# Revit family: YGNIS_Caldera de condensación LRK
name_source: partatom
category: Equipos mecánicos
revit_build: Autodesk Revit 2016 (Build: 20150220_1215(x64)
units: mm (PartAtom-declared; Revit-internal decimal feet)

## family parameters
Compartido = No
Corte con vacíos al cargar = No
Cota de conector redondo = Diámetro de uso
Número OmniClass = 23.75.00.00
Punto de cálculo de habitación = No
Se basa en plano de trabajo = No
Siempre vertical = Sí
Tipo de pieza = Normal
Título OmniClass = Climate Control (HVAC)

## types (10) — shared parameters
Asas = 580 mm
Código de montaje = D3020100
Descripción = Calderas de condensación para gas
o gasóleo 3 pasos de humos
Fabricante = YGNIS Atlantic
Presión de servicio = 5.9 atm
URL = http://www.ygnis.es

## per-type parameters (varying)
- LRK 23: B=1180 mm; H=1450 mm; L=2700 mm; Modelo=LRK 23; Peso=1800.00 kg; Potencia 30/35ºC=709 kW; Potencia 80/60ºC=630 kW; Potencia útil condensador=79 kW; Volumen=690.0 L; a=145 mm  [stored 0.475722 ft]; b=1060 mm; c=800 mm; d1=690 mm; d2=240 mm  [stored 0.787402 ft]; e=250 mm  [stored 0.82021 ft]; e. ext=300 mm; e. int=245 mm  [stored 0.803806 ft]; f=60 mm  [stored 0.19685 ft]; g=100 mm  [stored 0.328084 ft]; h=1370 mm; i=150 mm; j=950 mm; k=100 mm  [stored 0.328084 ft]; l=1695 mm; m=285 mm; n=80 mm  [stored 0.262467 ft]; n.2=180 mm; o=475 mm; q=85 mm  [stored 0.278871 ft]; q.2=30 mm  [stored 0.0984252 ft]; ø empalme ida-retorno=200 mm  [stored 0.656168 ft]
- LRK 24: B=1250 mm; H=1535 mm; L=2960 mm; Modelo=LRK 24; Peso=2160.00 kg; Potencia 30/35ºC=787 kW; Potencia 80/60ºC=700 kW; Potencia útil condensador=87 kW; Volumen=840.0 L; a=145 mm  [stored 0.475722 ft]; b=1130 mm; c=875 mm; d1=740 mm; d2=305 mm  [stored 1.00066 ft]; e=250 mm  [stored 0.82021 ft]; e. ext=300 mm; e. int=245 mm  [stored 0.803806 ft]; f=60 mm  [stored 0.19685 ft]; g=100 mm  [stored 0.328084 ft]; h=1455 mm; i=200 mm  [stored 0.656168 ft]; j=1150 mm; k=115 mm  [stored 0.377297 ft]; l=1880 mm; m=305 mm  [stored 1.00066 ft]; n=80 mm  [stored 0.262467 ft]; n.2=180 mm; o=560 mm; q=125 mm  [stored 0.410105 ft]; q.2=70 mm  [stored 0.229659 ft]; ø empalme ida-retorno=200 mm  [stored 0.656168 ft]
- LRK 25: B=1250 mm; H=1535 mm; L=2960 mm; Modelo=LRK 25; Peso=2160.00 kg; Potencia 30/35ºC=901 kW; Potencia 80/60ºC=800 kW; Potencia útil condensador=101 kW; Volumen=840.0 L; a=145 mm  [stored 0.475722 ft]; b=1130 mm; c=875 mm; d1=740 mm; d2=305 mm  [stored 1.00066 ft]; e=250 mm  [stored 0.82021 ft]; e. ext=300 mm; e. int=245 mm  [stored 0.803806 ft]; f=60 mm  [stored 0.19685 ft]; g=100 mm  [stored 0.328084 ft]; h=1455 mm; i=200 mm  [stored 0.656168 ft]; j=1150 mm; k=115 mm  [stored 0.377297 ft]; l=1880 mm; m=305 mm  [stored 1.00066 ft]; n=80 mm  [stored 0.262467 ft]; n.2=180 mm; o=560 mm; q=125 mm  [stored 0.410105 ft]; q.2=70 mm  [stored 0.229659 ft]; ø empalme ida-retorno=200 mm  [stored 0.656168 ft]
- LRK 26: B=1330 mm; H=1625 mm; L=3130 mm; Modelo=LRK 26; Peso=2420.00 kg; Potencia 30/35ºC=1005 kW; Potencia 80/60ºC=895 kW; Potencia útil condensador=110 kW; Volumen=1020.0 L; a=145 mm  [stored 0.475722 ft]; b=1210 mm; c=950 mm; d1=790 mm; d2=355 mm; e=300 mm; e. ext=350 mm  [stored 1.14829 ft]; e. int=295 mm  [stored 0.967848 ft]; f=60 mm  [stored 0.19685 ft]; g=100 mm  [stored 0.328084 ft]; h=1545 mm; i=200 mm  [stored 0.656168 ft]; j=1150 mm; k=125 mm  [stored 0.410105 ft]; l=1975 mm; m=335 mm  [stored 1.09908 ft]; n=100 mm  [stored 0.328084 ft]; n.2=200 mm  [stored 0.656168 ft]; o=650 mm; q=165 mm; q.2=110 mm  [stored 0.360892 ft]; ø empalme ida-retorno=200 mm  [stored 0.656168 ft]
- LRK 27: B=1420 mm; H=1730 mm; L=3624 mm; Modelo=LRK 27; Peso=2950.00 kg; Potencia 30/35ºC=1293 kW; Potencia 80/60ºC=1150 kW; Potencia útil condensador=143 kW; Volumen=1430.0 L; a=145 mm  [stored 0.475722 ft]; b=1300 mm; c=1105 mm; d1=840 mm; d2=400 mm; e=350 mm  [stored 1.14829 ft]; e. ext=400 mm; e. int=345 mm  [stored 1.13189 ft]; f=60 mm  [stored 0.19685 ft]; g=125 mm  [stored 0.410105 ft]; h=1650 mm; i=238 mm  [stored 0.78084 ft]; j=1493 mm; k=110 mm  [stored 0.360892 ft]; l=2314 mm; m=385 mm  [stored 1.26312 ft]; n=100 mm  [stored 0.328084 ft]; n.2=200 mm  [stored 0.656168 ft]; o=720 mm; q=185 mm  [stored 0.606955 ft]; q.2=130 mm  [stored 0.426509 ft]; ø empalme ida-retorno=225 mm  [stored 0.738189 ft]
- LRK 28: B=1420 mm; H=1730 mm; L=3624 mm; Modelo=LRK 28; Peso=2950.00 kg; Potencia 30/35ºC=1463 kW; Potencia 80/60ºC=1300 kW; Potencia útil condensador=164 kW; Volumen=1430.0 L; a=145 mm  [stored 0.475722 ft]; b=1300 mm; c=1105 mm; d1=840 mm; d2=400 mm; e=350 mm  [stored 1.14829 ft]; e. ext=400 mm; e. int=345 mm  [stored 1.13189 ft]; f=60 mm  [stored 0.19685 ft]; g=125 mm  [stored 0.410105 ft]; h=1650 mm; i=238 mm  [stored 0.78084 ft]; j=1493 mm; k=110 mm  [stored 0.360892 ft]; l=2314 mm; m=385 mm  [stored 1.26312 ft]; n=100 mm  [stored 0.328084 ft]; n.2=200 mm  [stored 0.656168 ft]; o=720 mm; q=185 mm  [stored 0.606955 ft]; q.2=130 mm  [stored 0.426509 ft]; ø empalme ida-retorno=225 mm  [stored 0.738189 ft]
- LRK 29: B=1495 mm; H=1805 mm; L=4194 mm; Modelo=LRK 29; Peso=3508.00 kg; Potencia 30/35ºC=1858 kW; Potencia 80/60ºC=1650 kW; Potencia útil condensador=208 kW; Volumen=1885.0 L; a=200 mm  [stored 0.656168 ft]; b=1375 mm; c=1260 mm; d1=875 mm; d2=448 mm; e=350 mm  [stored 1.14829 ft]; e. ext=400 mm; e. int=345 mm  [stored 1.13189 ft]; f=60 mm  [stored 0.19685 ft]; g=125 mm  [stored 0.410105 ft]; h=1725 mm; i=274 mm  [stored 0.89895 ft]; j=1727 mm; k=107 mm  [stored 0.35105 ft]; l=2374 mm; m=455 mm; n=125 mm  [stored 0.410105 ft]; n.2=225 mm  [stored 0.738189 ft]; o=795 mm; q=235 mm  [stored 0.770997 ft]; q.2=180 mm; ø empalme ida-retorno=225 mm  [stored 0.738189 ft]
- LRK 30: B=1565 mm; H=1870 mm; L=4579 mm; Modelo=LRK 30; Peso=4133.00 kg; Potencia 30/35ºC=2139 kW; Potencia 80/60ºC=1900 kW; Potencia útil condensador=239 kW; Volumen=2170.0 L; a=200 mm  [stored 0.656168 ft]; b=1445 mm; c=1360 mm; d1=905 mm; d2=400 mm; e=400 mm; e. ext=450 mm; e. int=395 mm; f=165 mm; g=150 mm; h=1790 mm; i=292 mm  [stored 0.958005 ft]; j=1844 mm; k=103 mm  [stored 0.337927 ft]; l=2854 mm; m=285 mm; n=125 mm  [stored 0.410105 ft]; n.2=225 mm  [stored 0.738189 ft]; o=780 mm; q=160 mm  [stored 0.524934 ft]; q.2=105 mm  [stored 0.344488 ft]; ø empalme ida-retorno=250 mm  [stored 0.82021 ft]
- LKR 31: B=1690 mm; H=1990 mm; L=4821 mm; Modelo=LRK 31; Peso=5169.00 kg; Potencia 30/35ºC=2813 kW; Potencia 80/60ºC=2500 kW; Potencia útil condensador=313 kW; Volumen=2755.0 L; a=200 mm  [stored 0.656168 ft]; b=1570 mm; c=1360 mm; d1=965 mm; d2=435 mm; e=450 mm; e. ext=500 mm; e. int=445 mm; f=165 mm; g=150 mm; h=1910 mm; i=318 mm  [stored 1.04331 ft]; j=2000 mm; k=100 mm  [stored 0.328084 ft]; l=3096 mm; m=285 mm; n=150 mm; n.2=250 mm  [stored 0.82021 ft]; o=860 mm; q=170 mm  [stored 0.557743 ft]; q.2=115 mm  [stored 0.377297 ft]; ø empalme ida-retorno=250 mm  [stored 0.82021 ft]
- LKR 32: B=1765 mm; H=2080 mm; L=5081 mm; Modelo=LRK 32; Peso=5892.00 kg; Potencia 30/35ºC=3378 kW; Potencia 80/60ºC=3000 kW; Potencia útil condensador=379 kW; Volumen=3240.0 L; a=200 mm  [stored 0.656168 ft]; b=1645 mm; c=1360 mm; d1=1015 mm; d2=490 mm; e=500 mm; e. ext=550 mm; e. int=495 mm; f=165 mm; g=200 mm  [stored 0.656168 ft]; h=2000 mm; i=344 mm  [stored 1.12861 ft]; j=2168 mm; k=110 mm  [stored 0.360892 ft]; l=3356 mm; m=285 mm; n=150 mm; n.2=250 mm  [stored 0.82021 ft]; o=940 mm; q=200 mm  [stored 0.656168 ft]; q.2=145 mm  [stored 0.475722 ft]; ø empalme ida-retorno=300 mm

note: [stored X ft] marks values corroborated as IEEE doubles in the binary element streams (Revit-internal decimal feet)

## geometry (parser evidence)
native form markers: Blend x1
no freeform markers — native parametric forms only
